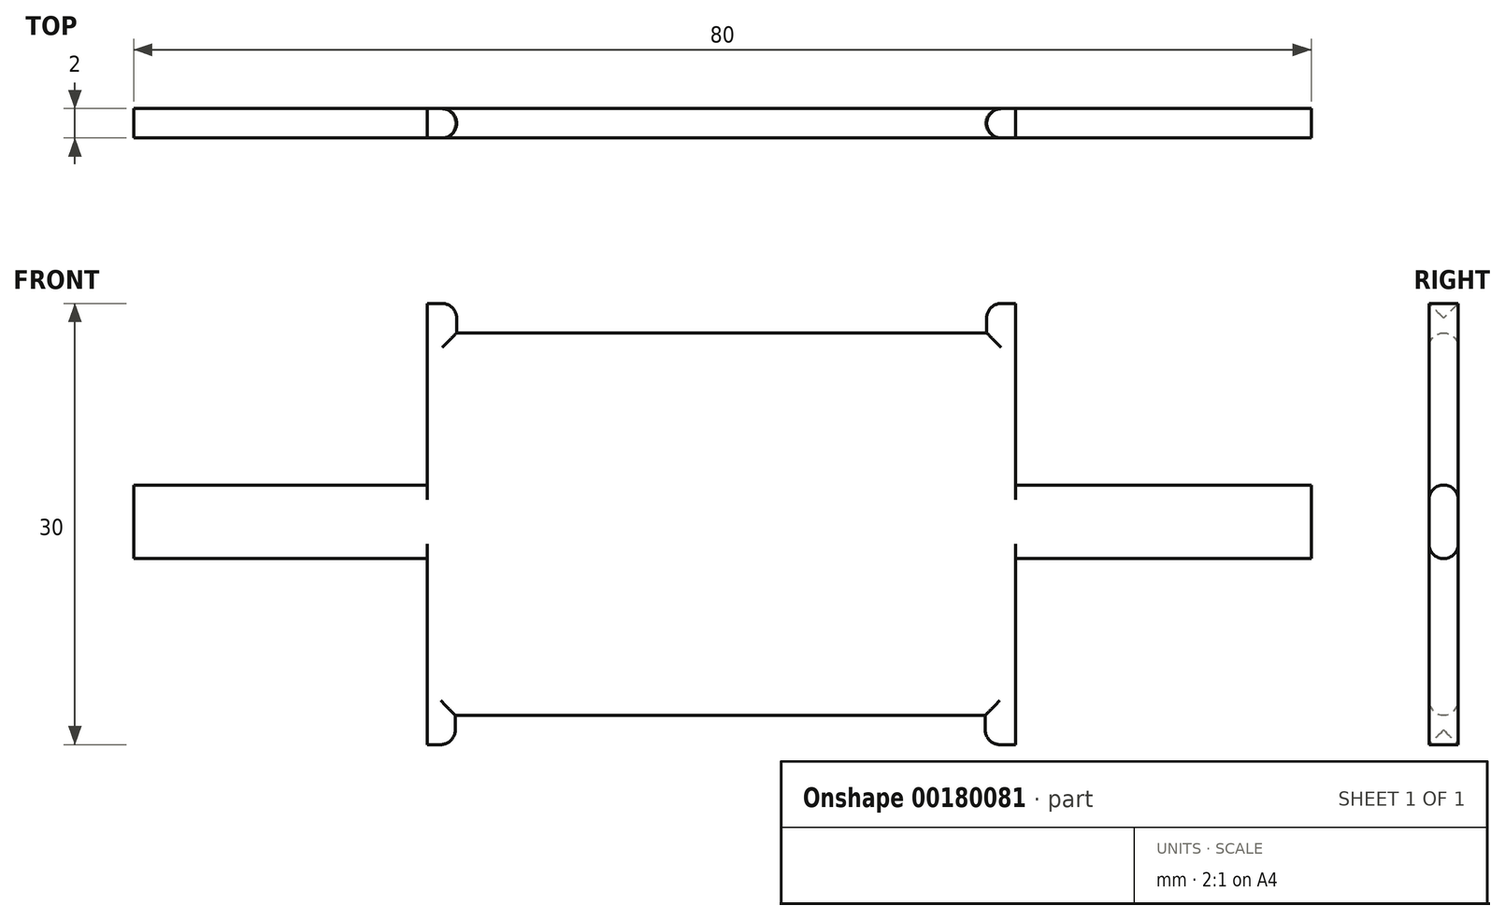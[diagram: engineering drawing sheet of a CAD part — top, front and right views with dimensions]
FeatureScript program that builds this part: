
annotation { "Feature Type Name" : "Feature", "Feature Type Description" : "" }
export const myFeature = defineFeature(function(context is Context, id is Id, definition is map)
    precondition{}
    {
        {
            var Q0;
            Q0=qCreatedBy(makeId("Front.planeOp"),FACE);
            var sketch = newSketch(context, id + "F0", { "sketchPlane" : qUnion([Q0])});
            skLineSegment(sketch, "E0.bottom", {"start": v(-20, 15) * mm, "end": v(20, 15) * mm});
            skLineSegment(sketch, "E0.top", {"start": v(-20, -15) * mm, "end": v(20, -15) * mm});
            skLineSegment(sketch, "E0.left", {"start": v(-20, 15) * mm, "end": v(-20, -15) * mm});
            skLineSegment(sketch, "E0.right", {"start": v(20, 15) * mm, "end": v(20, -15) * mm});
            skPoint(sketch, "E0.middle", {"position": v(0, 0) * mm});
            skLineSegment(sketch, "E1.bottom", {"start": v(-39.93, 2.65) * mm, "end": v(40.07, 2.65) * mm});
            skLineSegment(sketch, "E1.top", {"start": v(-39.93, -2.35) * mm, "end": v(40.07, -2.35) * mm});
            skLineSegment(sketch, "E1.left", {"start": v(-39.93, 2.65) * mm, "end": v(-39.93, -2.35) * mm});
            skLineSegment(sketch, "E1.right", {"start": v(40.07, 2.65) * mm, "end": v(40.07, -2.35) * mm});
            skLineSegment(sketch, "E2.bottom", {"start": v(-17.98, 15) * mm, "end": v(18.02, 15) * mm});
            skLineSegment(sketch, "E2.top", {"start": v(-17.98, 13) * mm, "end": v(18.02, 13) * mm});
            skLineSegment(sketch, "E2.left", {"start": v(-17.98, 15) * mm, "end": v(-17.98, 13) * mm});
            skLineSegment(sketch, "E2.right", {"start": v(18.02, 15) * mm, "end": v(18.02, 13) * mm});
            skLineSegment(sketch, "E3.bottom", {"start": v(-18.08, -15) * mm, "end": v(17.92, -15) * mm});
            skLineSegment(sketch, "E3.top", {"start": v(-18.08, -13) * mm, "end": v(17.92, -13) * mm});
            skLineSegment(sketch, "E3.left", {"start": v(-18.08, -15) * mm, "end": v(-18.08, -13) * mm});
            skLineSegment(sketch, "E3.right", {"start": v(17.92, -15) * mm, "end": v(17.92, -13) * mm});
            skSolve(sketch);
        }
        {
            var Q0;
            Q0=makeQuery(id+"F0.imprint","IMPRINT",FACE,{"disambiguationData":[TD([[makeQuery(id+"F0.imprint","IMPRINT",EDGE,{"derivedFrom":sQuery(id+"F0.wireOp",EDGE,"E2.top")}),-1.0]])]});
            var Q1;
            {var subQ0=sQuery(id+"F0.wireOp",EDGE,"E1.bottom");var subQ1=sQuery(id+"F0.wireOp",EDGE,"E0.left");var subQ2=makeQuery(id+"F0.imprint","INTERSECT",VERTEX,{"derivedFrom":[subQ1,subQ0]});Q1=makeQuery(id+"F0.imprint","IMPRINT",FACE,{"disambiguationData":[TD([[makeQuery(id+"F0.imprint","IMPRINT",EDGE,{"disambiguationData":[TD([[subQ2,-1.0]])],"derivedFrom":subQ1}),1.0]])]});}
            var Q2;
            {var subQ5=sQuery(id+"F0.wireOp",EDGE,"E1.right");Q2=makeQuery(id+"F0.imprint","IMPRINT",FACE,{"disambiguationData":[TD([[makeQuery(id+"F0.imprint","IMPRINT",EDGE,{"derivedFrom":subQ5}),-1.0]])]});}
            var Q3;
            {var subQ5=sQuery(id+"F0.wireOp",EDGE,"E1.left");Q3=makeQuery(id+"F0.imprint","IMPRINT",FACE,{"disambiguationData":[TD([[makeQuery(id+"F0.imprint","IMPRINT",EDGE,{"derivedFrom":subQ5}),1.0]])]});}
            var Q4;
            Q4=makeQuery(id+"F0.imprint","IMPRINT",FACE,{"disambiguationData":[TD([[makeQuery(id+"F0.imprint","IMPRINT",EDGE,{"derivedFrom":sQuery(id+"F0.wireOp",EDGE,"E3.top")}),1.0]])]});
            extrude(context, id + "F1", {"entities" : qUnion([Q0, Q1, Q2, Q3, Q4]), "depth" : 2 * mm});
        }
        {
            var Q0;
            {var subQ0=sQuery(id+"F0.wireOp",EDGE,"E1.top");Q0=makeQuery(id+"F1.opExtrude","CAP_EDGE",EDGE,{"disambiguationData":[OSD([subQ0]),TDD([makeQuery(id+"F0.imprint","IMPRINT",EDGE,{"disambiguationData":[TD([[makeQuery(id+"F0.imprint","INTERSECT",VERTEX,{"derivedFrom":[subQ0,sQuery(id+"F0.wireOp",EDGE,"E1.right")]}),1.0]])],"derivedFrom":subQ0})])],"isStart":false});}
            var Q1;
            {var subQ0=sQuery(id+"F0.wireOp",EDGE,"E1.top");Q1=makeQuery(id+"F1.opExtrude","CAP_EDGE",EDGE,{"disambiguationData":[OSD([subQ0]),TDD([makeQuery(id+"F0.imprint","IMPRINT",EDGE,{"disambiguationData":[TD([[makeQuery(id+"F0.imprint","INTERSECT",VERTEX,{"derivedFrom":[subQ0,sQuery(id+"F0.wireOp",EDGE,"E1.right")]}),1.0]])],"derivedFrom":subQ0})])],"isStart":true});}
            var Q2;
            {var subQ0=sQuery(id+"F0.wireOp",EDGE,"E1.bottom");Q2=makeQuery(id+"F1.opExtrude","CAP_EDGE",EDGE,{"disambiguationData":[OSD([subQ0]),TDD([makeQuery(id+"F0.imprint","IMPRINT",EDGE,{"disambiguationData":[TD([[makeQuery(id+"F0.imprint","INTERSECT",VERTEX,{"derivedFrom":[subQ0,sQuery(id+"F0.wireOp",EDGE,"E1.right")]}),1.0]])],"derivedFrom":subQ0})])],"isStart":false});}
            var Q3;
            {var subQ0=sQuery(id+"F0.wireOp",EDGE,"E1.bottom");Q3=makeQuery(id+"F1.opExtrude","CAP_EDGE",EDGE,{"disambiguationData":[OSD([subQ0]),TDD([makeQuery(id+"F0.imprint","IMPRINT",EDGE,{"disambiguationData":[TD([[makeQuery(id+"F0.imprint","INTERSECT",VERTEX,{"derivedFrom":[subQ0,sQuery(id+"F0.wireOp",EDGE,"E1.left")]}),-1.0]])],"derivedFrom":subQ0})])],"isStart":true});}
            var Q4;
            {var subQ0=sQuery(id+"F0.wireOp",EDGE,"E1.bottom");Q4=makeQuery(id+"F1.opExtrude","CAP_EDGE",EDGE,{"disambiguationData":[OSD([subQ0]),TDD([makeQuery(id+"F0.imprint","IMPRINT",EDGE,{"disambiguationData":[TD([[makeQuery(id+"F0.imprint","INTERSECT",VERTEX,{"derivedFrom":[subQ0,sQuery(id+"F0.wireOp",EDGE,"E1.left")]}),-1.0]])],"derivedFrom":subQ0})])],"isStart":false});}
            var Q5;
            {var subQ0=sQuery(id+"F0.wireOp",EDGE,"E1.top");Q5=makeQuery(id+"F1.opExtrude","CAP_EDGE",EDGE,{"disambiguationData":[OSD([subQ0]),TDD([makeQuery(id+"F0.imprint","IMPRINT",EDGE,{"disambiguationData":[TD([[makeQuery(id+"F0.imprint","INTERSECT",VERTEX,{"derivedFrom":[subQ0,sQuery(id+"F0.wireOp",EDGE,"E1.left")]}),-1.0]])],"derivedFrom":subQ0})])],"isStart":true});}
            var Q6;
            {var subQ0=sQuery(id+"F0.wireOp",EDGE,"E1.bottom");Q6=makeQuery(id+"F1.opExtrude","CAP_EDGE",EDGE,{"disambiguationData":[OSD([subQ0]),TDD([makeQuery(id+"F0.imprint","IMPRINT",EDGE,{"disambiguationData":[TD([[makeQuery(id+"F0.imprint","INTERSECT",VERTEX,{"derivedFrom":[subQ0,sQuery(id+"F0.wireOp",EDGE,"E1.right")]}),1.0]])],"derivedFrom":subQ0})])],"isStart":true});}
            var Q7;
            {var subQ0=sQuery(id+"F0.wireOp",EDGE,"E1.top");Q7=makeQuery(id+"F1.opExtrude","CAP_EDGE",EDGE,{"disambiguationData":[OSD([subQ0]),TDD([makeQuery(id+"F0.imprint","IMPRINT",EDGE,{"disambiguationData":[TD([[makeQuery(id+"F0.imprint","INTERSECT",VERTEX,{"derivedFrom":[subQ0,sQuery(id+"F0.wireOp",EDGE,"E1.left")]}),-1.0]])],"derivedFrom":subQ0})])],"isStart":false});}
            fillet(context, id + "F2", {"entities" : qUnion([Q0, Q1, Q2, Q3, Q4, Q5, Q6, Q7]), "radius" : 1 * mm, "tangentPropagation" : true, "allowEdgeOverflow" : false});
        }
        {
            var Q0;
            Q0=makeQuery(id+"F1.opExtrude","CAP_EDGE",EDGE,{"disambiguationData":[OSD([sQuery(id+"F0.wireOp",EDGE,"E3.top")])],"isStart":false});
            var Q1;
            Q1=makeQuery(id+"F1.opExtrude","CAP_EDGE",EDGE,{"disambiguationData":[OSD([sQuery(id+"F0.wireOp",EDGE,"E3.top")])],"isStart":true});
            var Q2;
            Q2=makeQuery(id+"F1.opExtrude","CAP_EDGE",EDGE,{"disambiguationData":[OSD([sQuery(id+"F0.wireOp",EDGE,"E2.top")])],"isStart":true});
            var Q3;
            Q3=makeQuery(id+"F1.opExtrude","CAP_EDGE",EDGE,{"disambiguationData":[OSD([sQuery(id+"F0.wireOp",EDGE,"E2.top")])],"isStart":false});
            fillet(context, id + "F3", {"entities" : qUnion([Q0, Q1, Q2, Q3]), "radius" : 1 * mm, "tangentPropagation" : true, "allowEdgeOverflow" : false});
        }
        {
            var Q0;
            Q0=makeQuery(id+"F1.opExtrude","CAP_EDGE",EDGE,{"disambiguationData":[OSD([sQuery(id+"F0.wireOp",EDGE,"E2.right")])],"isStart":false});
            var Q1;
            Q1=makeQuery(id+"F1.opExtrude","SWEPT_EDGE",EDGE,{"disambiguationData":[OSD([sQuery(id+"F0.wireOp",EDGE,"E0.bottom"),sQuery(id+"F0.wireOp",EDGE,"E2.bottom"),sQuery(id+"F0.wireOp",EDGE,"E2.right")])]});
            var Q2;
            Q2=makeQuery(id+"F1.opExtrude","CAP_EDGE",EDGE,{"disambiguationData":[OSD([sQuery(id+"F0.wireOp",EDGE,"E2.right")])],"isStart":true});
            var Q3;
            Q3=makeQuery(id+"F1.opExtrude","CAP_EDGE",EDGE,{"disambiguationData":[OSD([sQuery(id+"F0.wireOp",EDGE,"E2.left")])],"isStart":false});
            var Q4;
            Q4=makeQuery(id+"F1.opExtrude","SWEPT_EDGE",EDGE,{"disambiguationData":[OSD([sQuery(id+"F0.wireOp",EDGE,"E0.bottom"),sQuery(id+"F0.wireOp",EDGE,"E2.bottom"),sQuery(id+"F0.wireOp",EDGE,"E2.left")])]});
            var Q5;
            Q5=makeQuery(id+"F1.opExtrude","CAP_EDGE",EDGE,{"disambiguationData":[OSD([sQuery(id+"F0.wireOp",EDGE,"E3.left")])],"isStart":false});
            var Q6;
            Q6=makeQuery(id+"F1.opExtrude","CAP_EDGE",EDGE,{"disambiguationData":[OSD([sQuery(id+"F0.wireOp",EDGE,"E3.right")])],"isStart":false});
            var Q7;
            Q7=makeQuery(id+"F1.opExtrude","CAP_EDGE",EDGE,{"disambiguationData":[OSD([sQuery(id+"F0.wireOp",EDGE,"E2.left")])],"isStart":true});
            var Q8;
            Q8=makeQuery(id+"F1.opExtrude","CAP_EDGE",EDGE,{"disambiguationData":[OSD([sQuery(id+"F0.wireOp",EDGE,"E3.left")])],"isStart":true});
            var Q9;
            Q9=makeQuery(id+"F1.opExtrude","SWEPT_EDGE",EDGE,{"disambiguationData":[OSD([sQuery(id+"F0.wireOp",EDGE,"E0.top"),sQuery(id+"F0.wireOp",EDGE,"E3.bottom"),sQuery(id+"F0.wireOp",EDGE,"E3.left")])]});
            var Q10;
            Q10=makeQuery(id+"F1.opExtrude","CAP_EDGE",EDGE,{"disambiguationData":[OSD([sQuery(id+"F0.wireOp",EDGE,"E3.right")])],"isStart":true});
            var Q11;
            Q11=makeQuery(id+"F1.opExtrude","SWEPT_EDGE",EDGE,{"disambiguationData":[OSD([sQuery(id+"F0.wireOp",EDGE,"E0.top"),sQuery(id+"F0.wireOp",EDGE,"E3.bottom"),sQuery(id+"F0.wireOp",EDGE,"E3.right")])]});
            fillet(context, id + "F4", {"entities" : qUnion([Q0, Q1, Q2, Q3, Q4, Q5, Q6, Q7, Q8, Q9, Q10, Q11]), "radius" : 1 * mm, "allowEdgeOverflow" : false});
        }
    });
